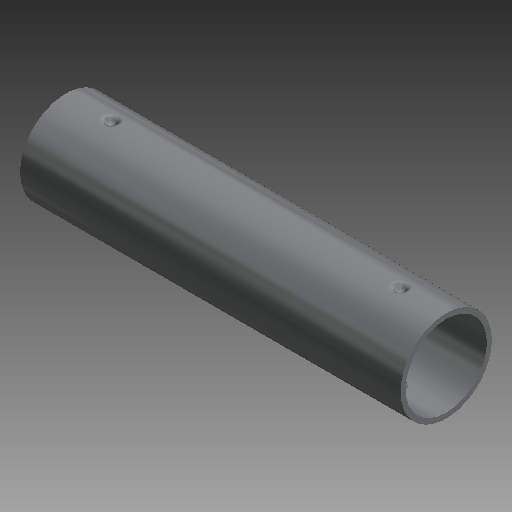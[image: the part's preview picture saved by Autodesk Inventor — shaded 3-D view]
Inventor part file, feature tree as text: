
AUTODESK INVENTOR PART (.ipt)
format: ipt  version: 2019 (Build 230136000, 136)  size: 161,280 bytes
history: native  units: mm (DEFAULTED — no unit token found)
features: mirror x1
ambient origin geometry x8: Origin, YZ Plane, XZ Plane, XY Plane, X Axis, Y Axis, Z Axis, Center Point
bodies: Solid1 (feature_tree)
feature tree (1):
  mirror  "Mirror2"
